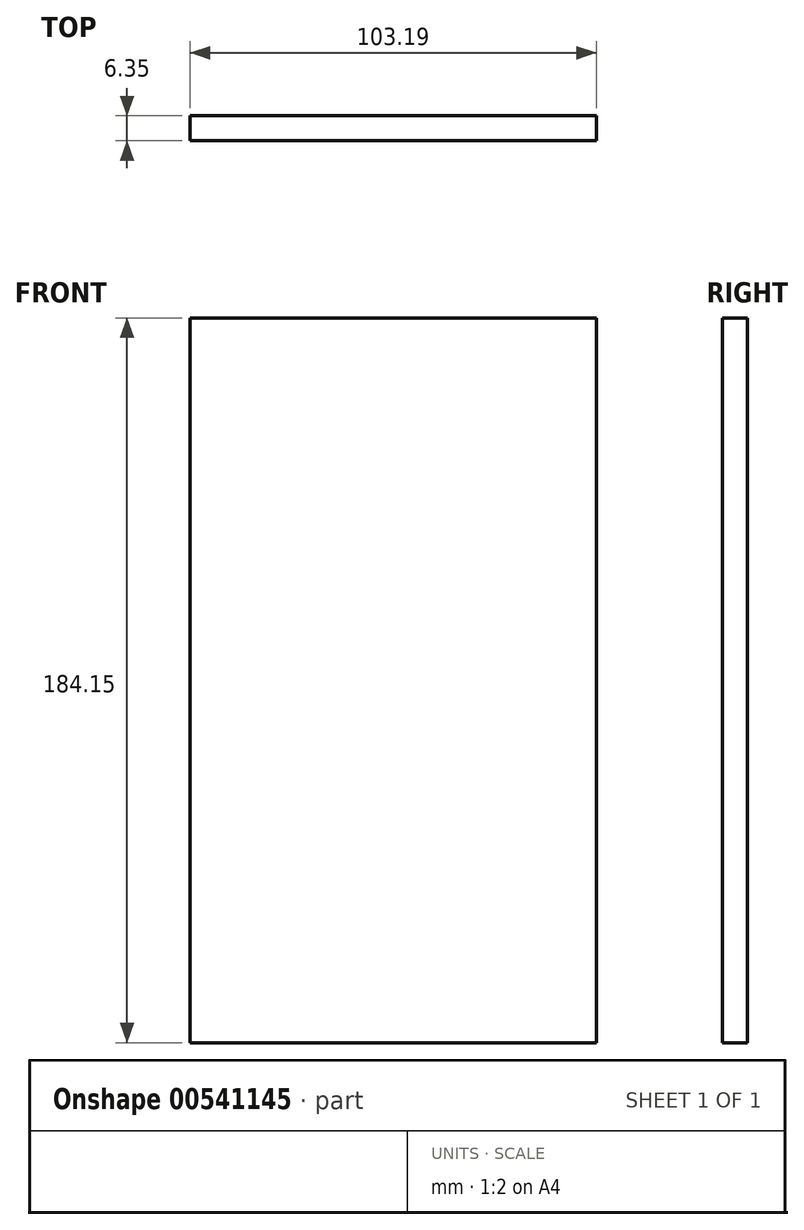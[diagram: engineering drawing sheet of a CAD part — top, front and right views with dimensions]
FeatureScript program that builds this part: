
annotation { "Feature Type Name" : "Feature", "Feature Type Description" : "" }
export const myFeature = defineFeature(function(context is Context, id is Id, definition is map)
    precondition{}
    {
        {
            var Q0;
            Q0=qCreatedBy(makeId("Front.planeOp"),FACE);
            var sketch = newSketch(context, id + "F0", { "sketchPlane" : qUnion([Q0])});
            skLineSegment(sketch, "E0.bottom", {"start": v(0, 0) * mm, "end": v(103.19, 0) * mm});
            skLineSegment(sketch, "E0.top", {"start": v(0, 184.15) * mm, "end": v(103.19, 184.15) * mm});
            skLineSegment(sketch, "E0.left", {"start": v(0, 0) * mm, "end": v(0, 184.15) * mm});
            skLineSegment(sketch, "E0.right", {"start": v(103.19, 0) * mm, "end": v(103.19, 184.15) * mm});
            skSolve(sketch);
        }
        {
            var Q0;
            Q0=makeQuery(id+"F0.imprint","IMPRINT",FACE,{"disambiguationData":[TD([[makeQuery(id+"F0.imprint","IMPRINT",EDGE,{"derivedFrom":sQuery(id+"F0.wireOp",EDGE,"E0.bottom")}),1.0]])]});
            extrude(context, id + "F1", {"entities" : qUnion([Q0]), "depth" : 6.35 * mm, "offsetDistance" : 25.4 * mm});
        }
    });
